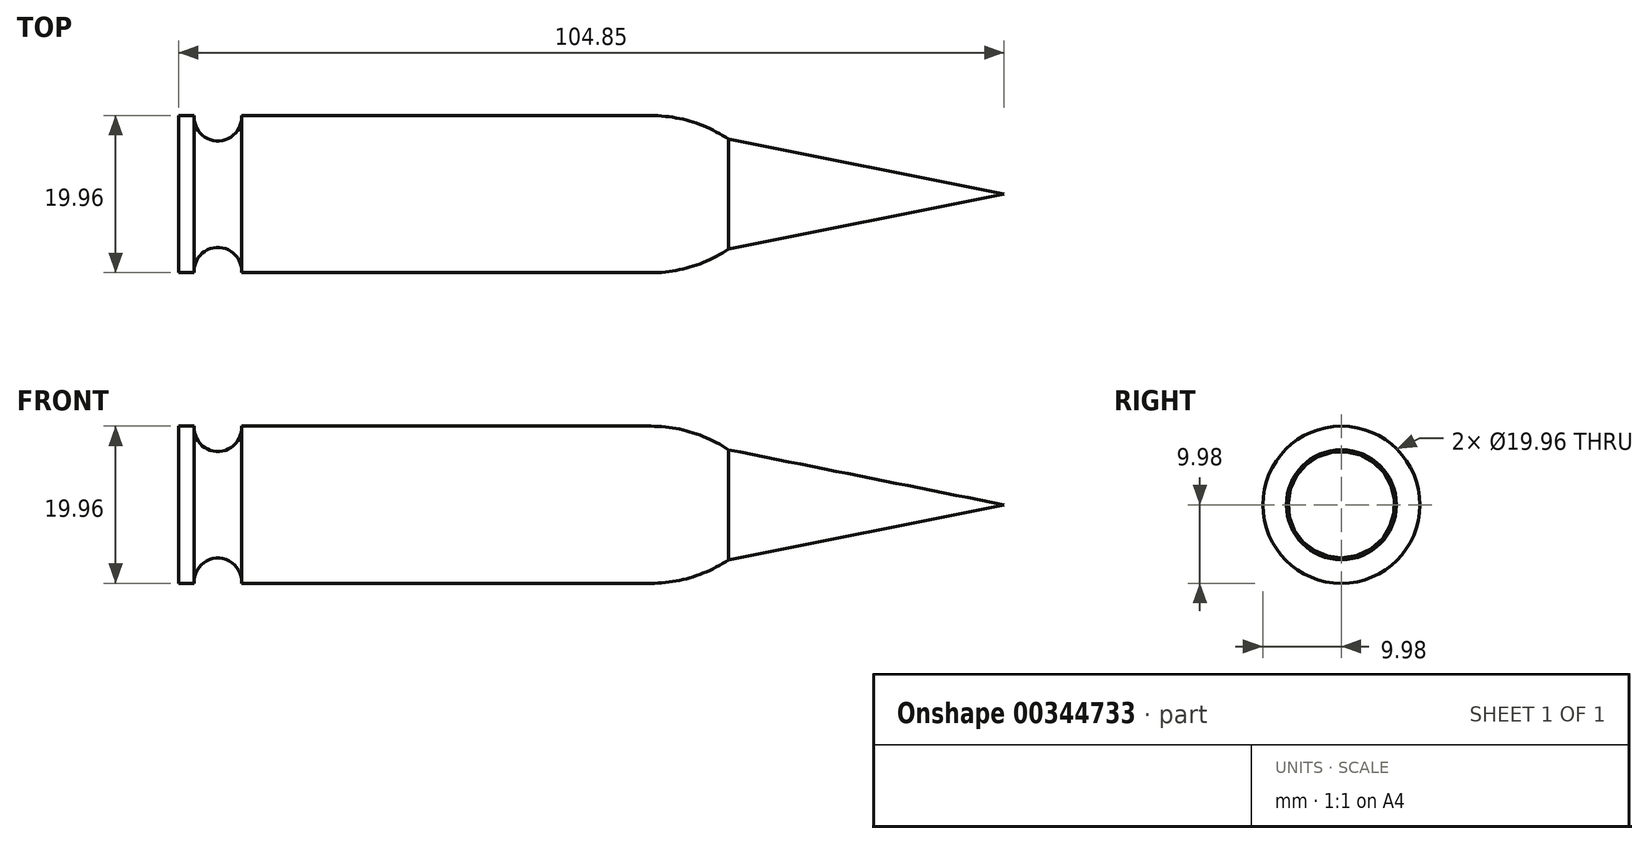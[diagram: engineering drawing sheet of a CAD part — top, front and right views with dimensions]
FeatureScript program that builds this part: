
annotation { "Feature Type Name" : "Feature", "Feature Type Description" : "" }
export const myFeature = defineFeature(function(context is Context, id is Id, definition is map)
    precondition{}
    {
        {
            var Q0;
            Q0=qCreatedBy(makeId("Front.planeOp"),FACE);
            var sketch = newSketch(context, id + "F0", { "sketchPlane" : qUnion([Q0])});
            skPoint(sketch, "E0", {"position": v(0, 9.98) * mm});
            skPoint(sketch, "E1", {"position": v(2, 9.98) * mm});
            skPoint(sketch, "E2", {"position": v(7.99, 9.98) * mm});
            skArc(sketch, "E3", {"start": v(2, 9.98) * mm, "mid": v(5, 6.76) * mm, "end": v(7.99, 9.98) * mm});
            skLineSegment(sketch, "E4", {"start": v(7.99, 9.98) * mm, "end": v(10.12, 9.98) * mm});
            skLineSegment(sketch, "E5", {"start": v(0, 9.98) * mm, "end": v(2, 9.98) * mm});
            skLineSegment(sketch, "E6", {"start": v(0, 9.98) * mm, "end": v(0, 0) * mm});
            skLineSegment(sketch, "E7", {"start": v(10.12, 9.98) * mm, "end": v(60.02, 9.98) * mm});
            skPoint(sketch, "E8", {"position": v(69.85, 6.98) * mm});
            skArc(sketch, "E9", {"start": v(60.02, 9.98) * mm, "mid": v(65.16, 9.21) * mm, "end": v(69.85, 6.98) * mm});
            skLineSegment(sketch, "E10", {"start": v(69.85, 6.98) * mm, "end": v(104.85, 0) * mm});
            skSolve(sketch);
        }
        {
            var Q0;
            Q0=qCreatedBy(makeId("Front.planeOp"),FACE);
            var sketch = newSketch(context, id + "F1", { "sketchPlane" : qUnion([Q0])});
            skLineSegment(sketch, "E11", {"start": v(112.51, 0) * mm, "end": v(124.27, 0) * mm});
            skSolve(sketch);
        }
        {
            var Q0;
            Q0 = qConstructionFilter(qBodyType(qCreatedBy(id + "F0" ,EDGE), BodyType.WIRE), ConstructionObject.NO);
            var Q1;
            Q1=sQuery(id+"F1.wireOp",EDGE,"E11");
            revolve(context, id + "F2", {"bodyType" : ToolBodyType.SURFACE, "surfaceEntities" : qUnion([Q0]), "axis" : qUnion([Q1]), "revolveType" : RevolveType.FULL});
        }
    });
